# Revit family: Hager-Golf-IP40-Plain_Door-syst-NL-en
name_source: partatom
category: Electrical Equipment
units: mm (PartAtom-declared; Revit-internal decimal feet)

## family parameters
Cut with Voids When Loaded = No
Host = Face
Panel Configuration = Two Columns, Circuits Across
Part Type = Panelboard
Room Calculation Point = No
Round Connector Dimension = Use Diameter
Shared = No

## types (6) — shared parameters
EF000007 - Colour = EV000202 - White
EF000116 - RAL-number = 9010
EF000118 - With mounting plate = No
EF000339 - Type of cover = EV004216 - Door
EF001062 - EMC-version = No
EF001088 - Extension possible = Yes
EF001134 - DIN-rail = Yes
EF001596 - Material housing = EV000139 - Plastic
EF002950 - Width in number of modular spacings = 12
EF004462 - Type of closure = EV000154 - Other
EF005474 - Degree of protection (IP) = EV006415 - IP40
EF006244 - Transparent cover/door = No
EF006306 - With lock = No
EF009212 - Cover model = EV000116 - Closed
EF015776 - Earthing terminal block = Yes
EF015777 - Neutral terminal block = No
EF015941 - Signal passing door = Yes
HG000001 - Number of columns = 1
HG000002 - With door or cover = Yes
HG000003 - Range = Golf
HG000005 - Thickness = 3 mm  [stored 0.00984252 ft]
HG000009 - Double swing door = No
HG000010 - Asymmetric doors = No
HG000011 - Empty rows from bottom = No
HG000017 - Distance between poles = 18 mm  [stored 0.0590551 ft]
Manufacturer = Hager
Type Comments = Golf
zero-valued in all types: Default Elevation, HG000007 - Number of empty columns, HG000008 - Number of empty rows

## per-type parameters (varying)
| type | EF000003 - Mounting method | EF000008 - Width | EF000040 - Height | EF000049 - Depth | EF000218 - Built-in depth | EF000266 - Number of rows | EF000332 - Built-in height | EF000846 - Built-in width | EF001131 - Internal depth | HG000004 - Manufacturer reference | HG000006 - Flush mounted | Model |
| Recessed mounted IP40 W352 H293 D97.5 12 Modular spacings - VF112PF | EV000383 - Flush mounted (plaster) | 352 mm | 293 mm | 98 mm | 72 mm  [stored 0.23622 ft] | 1 | 257 mm | 318 mm | 98 mm | VF112PF | Yes | VF112PF |
| Recessed mounted IP40 W352 H543 D97.5 12 Modular spacings - VF312PF | EV000383 - Flush mounted (plaster) | 352 mm | 543 mm | 98 mm | 72 mm  [stored 0.23622 ft] | 3 | 507 mm | 318 mm | 98 mm | VF312PF | Yes | VF312PF |
| Recessed mounted IP40 W382 H418 D97.5 12 Modular spacings - VF212PF | EV000383 - Flush mounted (plaster) | 382 mm | 418 mm | 98 mm | 72 mm  [stored 0.23622 ft] | 2 | 382 mm | 318 mm | 98 mm | VF212PF | Yes | VF212PF |
| Surface mounted IP40 W282 H252 D99 12 Modular spacings - VS112PF | EV000384 - Surface mounted (plaster) | 282 mm  [stored 0.925197 ft] | 252 mm | 99 mm  [stored 0.324803 ft] | 0 mm  [stored 0 ft] | 1 | 0 mm  [stored 0 ft] | 0 mm  [stored 0 ft] | 99 mm  [stored 0.324803 ft] | VS112PF | No | VS112PF |
| Surface mounted IP40 W282 H377 D99 12 Modular spacings - VS212PF | EV000384 - Surface mounted (plaster) | 282 mm  [stored 0.925197 ft] | 377 mm | 99 mm  [stored 0.324803 ft] | 0 mm  [stored 0 ft] | 2 | 0 mm  [stored 0 ft] | 0 mm  [stored 0 ft] | 99 mm  [stored 0.324803 ft] | VS212PF | No | VS212PF |
| Surface mounted IP40 W282 H500 D99 12 Modular spacings - VS312PF | EV000384 - Surface mounted (plaster) | 282 mm  [stored 0.925197 ft] | 500 mm  [stored 1.64042 ft] | 99 mm  [stored 0.324803 ft] | 0 mm  [stored 0 ft] | 3 | 0 mm  [stored 0 ft] | 0 mm  [stored 0 ft] | 99 mm  [stored 0.324803 ft] | VS312PF | No | VS312PF |

note: [stored X ft] marks values corroborated as IEEE doubles in the binary element streams (Revit-internal decimal feet)

## geometry (parser evidence)
native form markers: Sweep x17
no freeform markers — native parametric forms only
